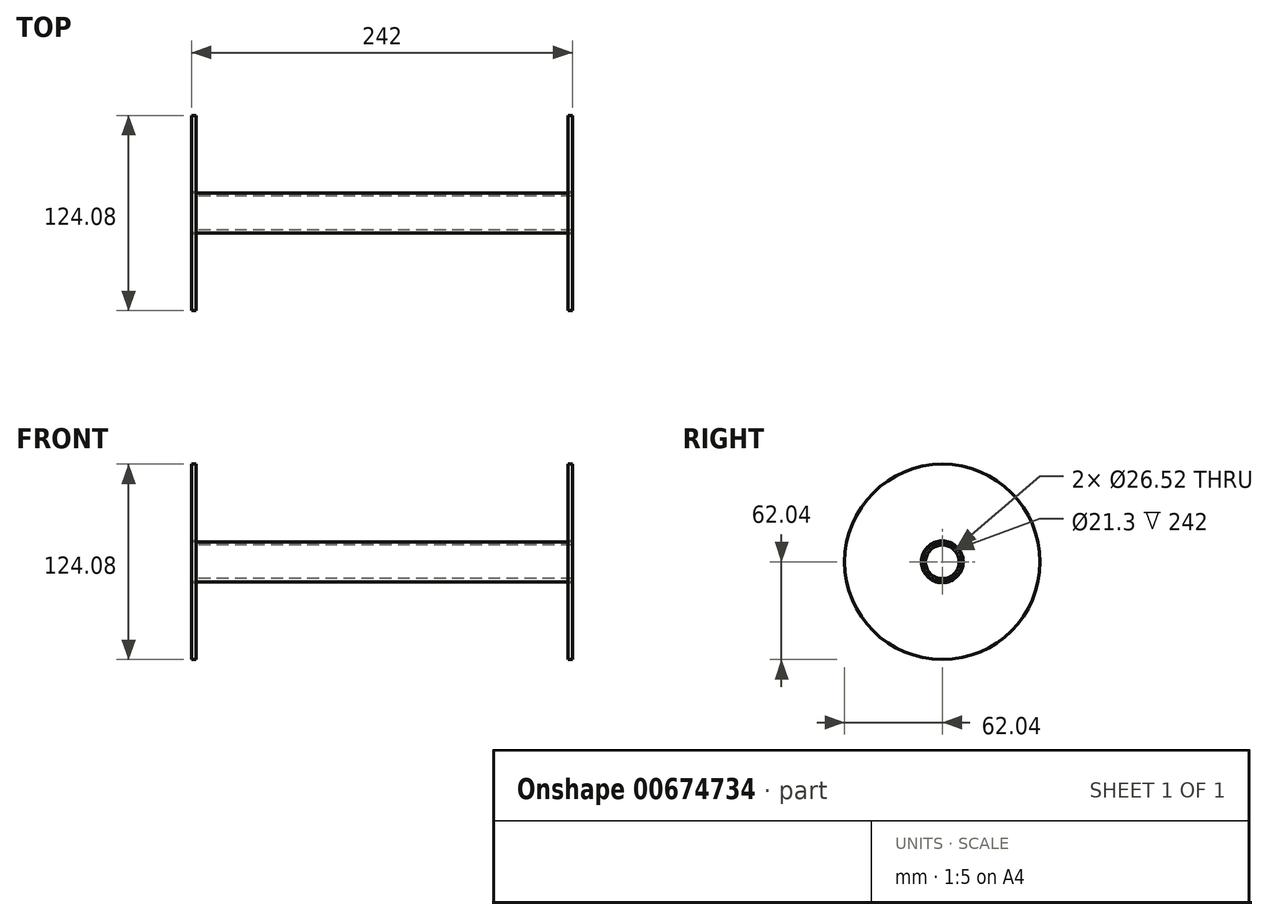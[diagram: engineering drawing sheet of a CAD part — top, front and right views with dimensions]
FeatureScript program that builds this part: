
annotation { "Feature Type Name" : "Feature", "Feature Type Description" : "" }
export const myFeature = defineFeature(function(context is Context, id is Id, definition is map)
    precondition{}
    {
        {
            var Q0;
            Q0=qCreatedBy(makeId("Right.planeOp"),FACE);
            var sketch = newSketch(context, id + "F0", { "sketchPlane" : qUnion([Q0])});
            skCircle(sketch, "E0", {"center": v(0, 0) * mm, "radius": 12.67 * mm});
            skCircle(sketch, "E1", {"center": v(0, 0) * mm, "radius": 10.65 * mm});
            skSolve(sketch);
        }
        {
            var Q0;
            Q0 = qSketchRegion(id + "F0", true);
            extrude(context, id + "F1", {"entities" : qUnion([Q0]), "endBound" : BoundingType.SYMMETRIC, "depth" : 242 * mm, "offsetDistance" : 25 * mm});
        }
        {
            var Q0;
            Q0=qCreatedBy(makeId("Front.planeOp"),FACE);
            var sketch = newSketch(context, id + "F2", { "sketchPlane" : qUnion([Q0])});
            skLineSegment(sketch, "E2", {"start": v(0, 0) * mm, "end": v(-136.5, 0) * mm, "construction": true});
            skLineSegment(sketch, "E3", {"start": v(0, 0) * mm, "end": v(127.2, 0) * mm, "construction": true});
            skLineSegment(sketch, "E4", {"start": v(0, 0) * mm, "end": v(0, 60.82) * mm, "construction": true});
            skSolve(sketch);
        }
        {
            var Q0;
            Q0=qCreatedBy(makeId("Front.planeOp"),FACE);
            var sketch = newSketch(context, id + "F3", { "sketchPlane" : qUnion([Q0])});
            skLineSegment(sketch, "E5", {"start": v(-120.96, 13.26) * mm, "end": v(120.8, 13.26) * mm, "construction": true});
            skLineSegment(sketch, "E6", {"start": v(-120.96, 13.26) * mm, "end": v(-120.96, 62.04) * mm});
            skLineSegment(sketch, "E7", {"start": v(-120.96, 62.04) * mm, "end": v(-118.21, 62.04) * mm});
            skLineSegment(sketch, "E8", {"start": v(-118.21, 62.04) * mm, "end": v(-118.21, 13.26) * mm});
            skLineSegment(sketch, "E9", {"start": v(-118.21, 13.26) * mm, "end": v(-120.96, 13.26) * mm});
            skLineSegment(sketch, "E10.MirrorCS", {"start": v(118.21, 13.26) * mm, "end": v(120.96, 13.26) * mm});
            skLineSegment(sketch, "E11.MirrorCS", {"start": v(120.96, 62.04) * mm, "end": v(118.21, 62.04) * mm});
            skLineSegment(sketch, "E12.MirrorCS", {"start": v(120.96, 13.26) * mm, "end": v(120.96, 62.04) * mm});
            skLineSegment(sketch, "E13.MirrorCS", {"start": v(118.21, 62.04) * mm, "end": v(118.21, 13.26) * mm});
            skSolve(sketch);
        }
        {
            var Q0;
            Q0 = qSketchRegion(id + "F3", true);
            var Q1;
            Q1=sQuery(id+"F2.wireOp",EDGE,"E3");
            revolve(context, id + "F4", {"operationType" : NewBodyOperationType.ADD, "entities" : qUnion([Q0]), "axis" : qUnion([Q1]), "revolveType" : RevolveType.FULL});
        }
    });
